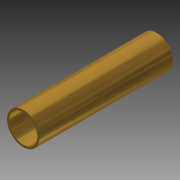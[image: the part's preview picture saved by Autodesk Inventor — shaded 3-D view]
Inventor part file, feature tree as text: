
AUTODESK INVENTOR PART (.ipt)
format: ipt  version: 2014 (Build 180170000, 170)  size: 80,896 bytes
history: native  units: in
note: dims shown in document units (in); Inventor stores cm internally (conversion verified against a paired STEP export)
features: extrude x1, sketch x1
ambient origin geometry x8: Origin, YZ Plane, XZ Plane, XY Plane, X Axis, Y Axis, Z Axis, Center Point
bodies: Solid1 (feature_tree)
feature tree (2):
  extrude  "Extrusion1"  Depth=1.8in
  sketch  "Sketch1"  dims[d0=0.379in d2=0.437in d3=1.8in d4=0.0in]
